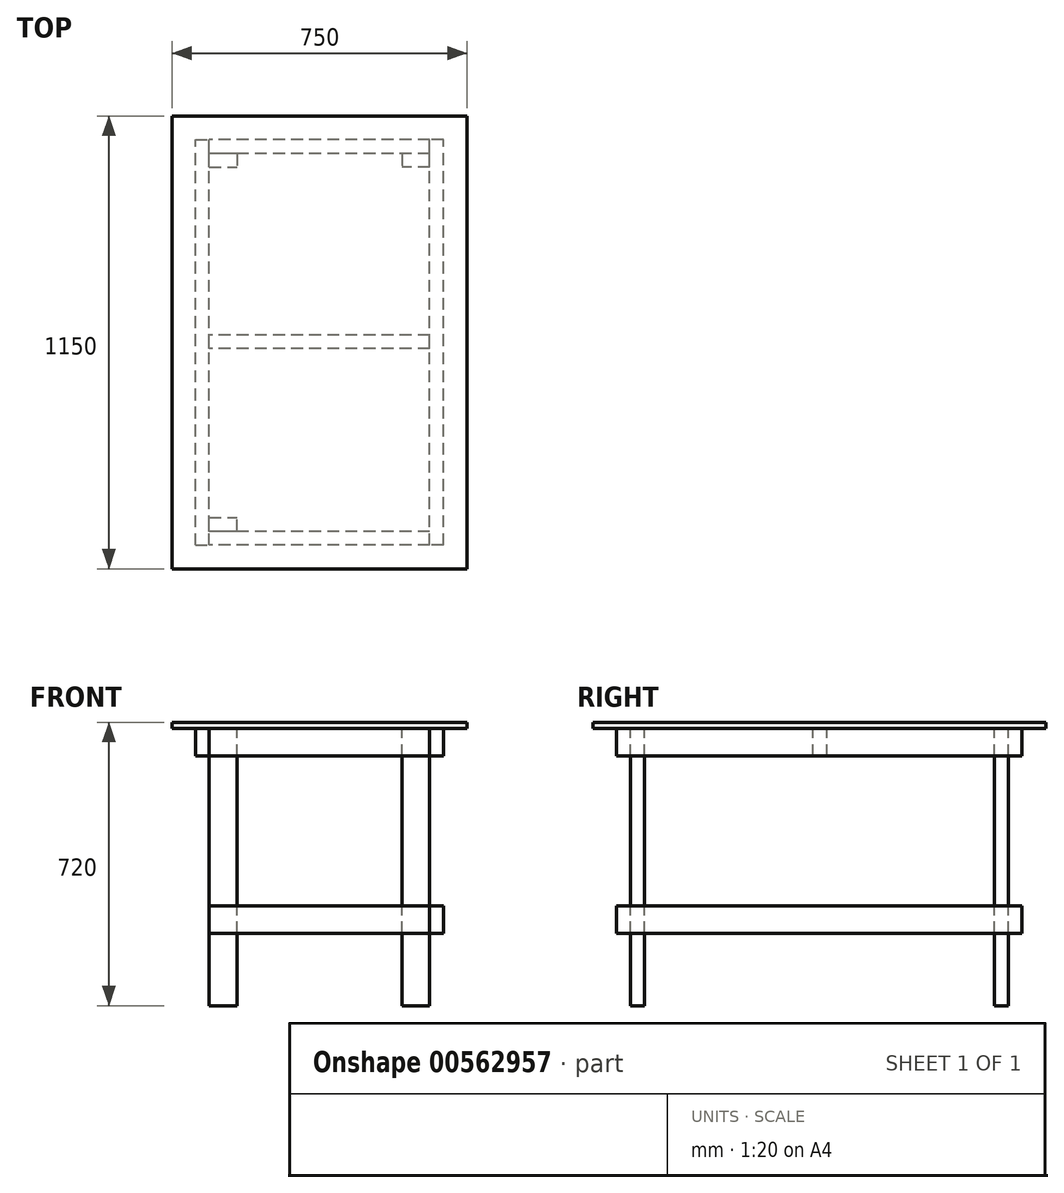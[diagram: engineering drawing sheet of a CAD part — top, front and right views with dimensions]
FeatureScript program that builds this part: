
annotation { "Feature Type Name" : "Feature", "Feature Type Description" : "" }
export const myFeature = defineFeature(function(context is Context, id is Id, definition is map)
    precondition{}
    {
        {
            var Q0;
            Q0=qCreatedBy(makeId("Top.planeOp"),FACE);
            var sketch = newSketch(context, id + "F0", { "sketchPlane" : qUnion([Q0])});
            skLineSegment(sketch, "E0.bottom", {"start": v(375, 575) * mm, "end": v(-375, 575) * mm});
            skLineSegment(sketch, "E0.top", {"start": v(375, -575) * mm, "end": v(-375, -575) * mm});
            skLineSegment(sketch, "E0.left", {"start": v(375, 575) * mm, "end": v(375, -575) * mm});
            skLineSegment(sketch, "E0.right", {"start": v(-375, 575) * mm, "end": v(-375, -575) * mm});
            skPoint(sketch, "E0.middle", {"position": v(0, 0) * mm});
            skLineSegment(sketch, "E1", {"start": v(0, -575) * mm, "end": v(0, 575) * mm, "construction": true});
            skLineSegment(sketch, "E2", {"start": v(-375, 0) * mm, "end": v(375, 0) * mm, "construction": true});
            skSolve(sketch);
        }
        {
            var Q0;
            Q0 = qSketchRegion(id + "F0", true);
            extrude(context, id + "F1", {"entities" : qUnion([Q0]), "depth" : 16 * mm, "offsetDistance" : 25 * mm});
        }
        {
            var Q0;
            Q0=qCreatedBy(makeId("Top.planeOp"),FACE);
            var sketch = newSketch(context, id + "F2", { "sketchPlane" : qUnion([Q0])});
            skLineSegment(sketch, "E3.0.0", {"start": v(-375, -575) * mm, "end": v(375, -575) * mm, "construction": true});
            skLineSegment(sketch, "E3.0.1", {"start": v(375, -575) * mm, "end": v(375, 575) * mm, "construction": true});
            skLineSegment(sketch, "E3.0.2", {"start": v(375, 575) * mm, "end": v(-375, 575) * mm, "construction": true});
            skLineSegment(sketch, "E3.0.3", {"start": v(-375, 575) * mm, "end": v(-375, -575) * mm, "construction": true});
            skLineSegment(sketch, "E4.0", {"start": v(315, 515) * mm, "end": v(-315, 515) * mm, "construction": true});
            skLineSegment(sketch, "E4.1", {"start": v(315, -515) * mm, "end": v(315, 515) * mm, "construction": true});
            skLineSegment(sketch, "E4.2", {"start": v(-315, -515) * mm, "end": v(315, -515) * mm, "construction": true});
            skLineSegment(sketch, "E4.3", {"start": v(-315, 515) * mm, "end": v(-315, -515) * mm, "construction": true});
            skLineSegment(sketch, "E5.bottom", {"start": v(315, -515) * mm, "end": v(280, -515) * mm});
            skLineSegment(sketch, "E5.top", {"start": v(315, 515) * mm, "end": v(280, 515) * mm});
            skLineSegment(sketch, "E5.left", {"start": v(315, -515) * mm, "end": v(315, 515) * mm});
            skLineSegment(sketch, "E5.right", {"start": v(280, -515) * mm, "end": v(280, 515) * mm});
            skLineSegment(sketch, "E6.bottom", {"start": v(280, -515) * mm, "end": v(-280, -515) * mm});
            skLineSegment(sketch, "E6.top", {"start": v(280, -480) * mm, "end": v(-280, -480) * mm});
            skLineSegment(sketch, "E6.left", {"start": v(280, -515) * mm, "end": v(280, -480) * mm});
            skLineSegment(sketch, "E6.right", {"start": v(-280, -515) * mm, "end": v(-280, -480) * mm});
            skLineSegment(sketch, "E7.bottom", {"start": v(280, -480) * mm, "end": v(210, -480) * mm});
            skLineSegment(sketch, "E7.top", {"start": v(280, -445) * mm, "end": v(210, -445) * mm});
            skLineSegment(sketch, "E7.left", {"start": v(280, -480) * mm, "end": v(280, -445) * mm});
            skLineSegment(sketch, "E7.right", {"start": v(210, -480) * mm, "end": v(210, -445) * mm});
            skLineSegment(sketch, "E8.MirrorCS", {"start": v(280, 445) * mm, "end": v(210, 445) * mm});
            skLineSegment(sketch, "E9.MirrorCS", {"start": v(210, 480) * mm, "end": v(210, 445) * mm});
            skLineSegment(sketch, "E10.MirrorCS", {"start": v(280, 480) * mm, "end": v(280, 445) * mm});
            skLineSegment(sketch, "E11.MirrorCS", {"start": v(280, 480) * mm, "end": v(210, 480) * mm});
            skLineSegment(sketch, "E12.MirrorCS", {"start": v(280, 480) * mm, "end": v(-280, 480) * mm});
            skLineSegment(sketch, "E13.MirrorCS", {"start": v(-280, -515) * mm, "end": v(-280, 515) * mm});
            skLineSegment(sketch, "E14.MirrorCS", {"start": v(-280, -445) * mm, "end": v(-210, -445) * mm});
            skLineSegment(sketch, "E15.MirrorCS", {"start": v(-210, -480) * mm, "end": v(-210, -445) * mm});
            skLineSegment(sketch, "E16.MirrorCS", {"start": v(-210, 480) * mm, "end": v(-210, 445) * mm});
            skLineSegment(sketch, "E17.MirrorCS", {"start": v(-280, 445) * mm, "end": v(-210, 445) * mm});
            skLineSegment(sketch, "E18.MirrorCS", {"start": v(-315, -515) * mm, "end": v(-315, 515) * mm});
            skLineSegment(sketch, "E19.MirrorCS", {"start": v(280, 515) * mm, "end": v(-280, 515) * mm});
            skLineSegment(sketch, "E20.MirrorCS", {"start": v(-315, -515) * mm, "end": v(-280, -515) * mm});
            skLineSegment(sketch, "E21.MirrorCS", {"start": v(-315, 515) * mm, "end": v(-280, 515) * mm});
            skSolve(sketch);
        }
        {
            var Q0;
            Q0=makeQuery(id+"F2.imprint","IMPRINT",FACE,{"disambiguationData":[TD([[makeQuery(id+"F2.imprint","IMPRINT",EDGE,{"derivedFrom":sQuery(id+"F2.wireOp",EDGE,"E7.bottom")}),-1.0]])]});
            var Q1;
            {var subQ4=sQuery(id+"F2.wireOp",EDGE,"E14.MirrorCS");Q1=makeQuery(id+"F2.imprint","IMPRINT",FACE,{"disambiguationData":[TD([[makeQuery(id+"F2.imprint","IMPRINT",EDGE,{"derivedFrom":subQ4}),-1.0]])]});}
            var Q2;
            {var subQ3=sQuery(id+"F2.wireOp",EDGE,"E16.MirrorCS");Q2=makeQuery(id+"F2.imprint","IMPRINT",FACE,{"disambiguationData":[TD([[makeQuery(id+"F2.imprint","IMPRINT",EDGE,{"derivedFrom":subQ3}),-1.0]])]});}
            var Q3;
            Q3=makeQuery(id+"F2.imprint","IMPRINT",FACE,{"disambiguationData":[TD([[makeQuery(id+"F2.imprint","IMPRINT",EDGE,{"derivedFrom":sQuery(id+"F2.wireOp",EDGE,"E8.MirrorCS")}),-1.0]])]});
            extrude(context, id + "F3", {"entities" : qUnion([Q0, Q1, Q2, Q3]), "oppositeDirection" : true, "depth" : 704 * mm, "offsetDistance" : 25 * mm});
        }
        {
            var Q0;
            {var subQ1=sQuery(id+"F2.wireOp",EDGE,"E6.bottom");Q0=makeQuery(id+"F2.imprint","IMPRINT",FACE,{"disambiguationData":[TD([[makeQuery(id+"F2.imprint","IMPRINT",EDGE,{"derivedFrom":subQ1}),-1.0]])]});}
            var Q1;
            {var subQ4=sQuery(id+"F2.wireOp",EDGE,"E19.MirrorCS");Q1=makeQuery(id+"F2.imprint","IMPRINT",FACE,{"disambiguationData":[TD([[makeQuery(id+"F2.imprint","IMPRINT",EDGE,{"derivedFrom":subQ4}),1.0]])]});}
            extrude(context, id + "F4", {"entities" : qUnion([Q0, Q1]), "oppositeDirection" : true, "depth" : 70 * mm, "offsetDistance" : 25 * mm});
        }
        {
            var Q0;
            Q0=makeQuery(id+"F2.imprint","IMPRINT",FACE,{"disambiguationData":[TD([[makeQuery(id+"F2.imprint","IMPRINT",EDGE,{"derivedFrom":sQuery(id+"F2.wireOp",EDGE,"E5.bottom")}),-1.0]])]});
            var Q1;
            Q1=makeQuery(id+"F2.imprint","IMPRINT",FACE,{"disambiguationData":[TD([[makeQuery(id+"F2.imprint","IMPRINT",EDGE,{"derivedFrom":sQuery(id+"F2.wireOp",EDGE,"E18.MirrorCS")}),-1.0]])]});
            extrude(context, id + "F5", {"entities" : qUnion([Q0, Q1]), "oppositeDirection" : true, "depth" : 70 * mm, "offsetDistance" : 25 * mm});
        }
        {
            var Q0;
            Q0=makeQuery(id+"F4.opExtrude","SWEPT_BODY",BODY,{"disambiguationData":[OSD([sQuery(id+"F2.wireOp",EDGE,"E6.bottom"),sQuery(id+"F2.wireOp",EDGE,"E6.top"),sQuery(id+"F2.wireOp",EDGE,"E6.left"),sQuery(id+"F2.wireOp",EDGE,"E7.bottom"),sQuery(id+"F2.wireOp",EDGE,"E13.MirrorCS")])]});
            var Q1;
            Q1=makeQuery(id+"F4.opExtrude","SWEPT_BODY",BODY,{"disambiguationData":[OSD([sQuery(id+"F2.wireOp",EDGE,"E5.right"),sQuery(id+"F2.wireOp",EDGE,"E12.MirrorCS"),sQuery(id+"F2.wireOp",EDGE,"E13.MirrorCS"),sQuery(id+"F2.wireOp",EDGE,"E19.MirrorCS")])]});
            var Q2;
            Q2=makeQuery(id+"F5.opExtrude","SWEPT_BODY",BODY,{"disambiguationData":[OSD([sQuery(id+"F2.wireOp",EDGE,"E5.bottom"),sQuery(id+"F2.wireOp",EDGE,"E5.top"),sQuery(id+"F2.wireOp",EDGE,"E5.left"),sQuery(id+"F2.wireOp",EDGE,"E5.right"),sQuery(id+"F2.wireOp",EDGE,"E6.left"),sQuery(id+"F2.wireOp",EDGE,"E7.left"),sQuery(id+"F2.wireOp",EDGE,"E10.MirrorCS")])]});
            var Q3;
            Q3=makeQuery(id+"F3.opExtrude","SWEPT_EDGE",EDGE,{"disambiguationData":[OSD([sQuery(id+"F2.wireOp",EDGE,"E6.top"),sQuery(id+"F2.wireOp",EDGE,"E13.MirrorCS")])]});
            var Q4;
            Q4=makeQuery(id+"F3.opExtrude","SWEPT_EDGE",EDGE,{"disambiguationData":[OSD([sQuery(id+"F2.wireOp",EDGE,"E6.top"),sQuery(id+"F2.wireOp",EDGE,"E13.MirrorCS")])]});
            transform(context, id + "F6", {"entities" : qUnion([Q0, Q1, Q2]), "transformType" : TransformType.TRANSLATION_DISTANCE, "transformDirection" : qUnion([Q4]), "distance" : 450 * mm, "oppositeDirection" : true, "makeCopy" : true});
        }
        {
            var Q0;
            Q0=makeQuery(id+"F4.opExtrude","SWEPT_BODY",BODY,{"disambiguationData":[OSD([sQuery(id+"F2.wireOp",EDGE,"E5.right"),sQuery(id+"F2.wireOp",EDGE,"E12.MirrorCS"),sQuery(id+"F2.wireOp",EDGE,"E13.MirrorCS"),sQuery(id+"F2.wireOp",EDGE,"E19.MirrorCS")])]});
            var Q1;
            Q1=makeQuery(id+"F5.opExtrude","CAP_EDGE",EDGE,{"disambiguationData":[OSD([sQuery(id+"F2.wireOp",EDGE,"E13.MirrorCS")])],"isStart":false});
            var Q2;
            Q2=makeQuery(id+"F5.opExtrude","CAP_EDGE",EDGE,{"disambiguationData":[OSD([sQuery(id+"F2.wireOp",EDGE,"E13.MirrorCS")])],"isStart":false});
            transform(context, id + "F7", {"entities" : qUnion([Q0]), "transformType" : TransformType.TRANSLATION_DISTANCE, "transformDirection" : qUnion([Q2]), "distance" : 496 * mm, "oppositeDirection" : true, "makeCopy" : true});
        }
    });
